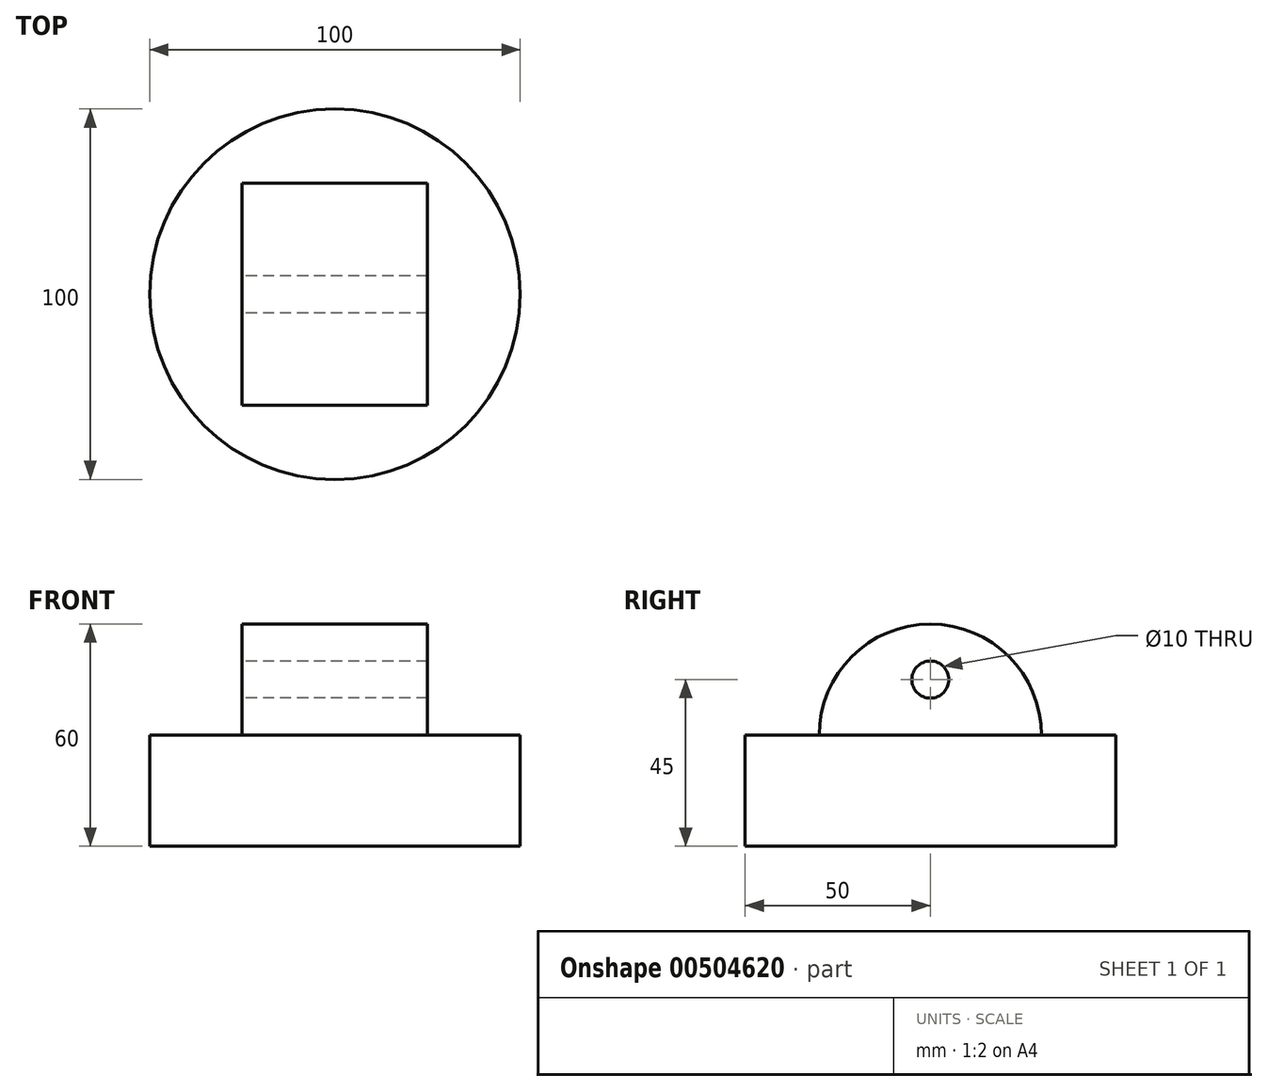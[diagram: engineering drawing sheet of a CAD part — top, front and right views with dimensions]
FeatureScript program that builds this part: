
annotation { "Feature Type Name" : "Feature", "Feature Type Description" : "" }
export const myFeature = defineFeature(function(context is Context, id is Id, definition is map)
    precondition{}
    {
        {
            var Q0;
            Q0=qCreatedBy(makeId("Top.planeOp"),FACE);
            var sketch = newSketch(context, id + "F0", { "sketchPlane" : qUnion([Q0])});
            skCircle(sketch, "E0", {"center": v(0, 0) * mm, "radius": 50 * mm});
            skLineSegment(sketch, "E1", {"start": v(0, 0) * mm, "end": v(0, 50) * mm});
            skSolve(sketch);
        }
        {
            var Q0;
            Q0=qSketchRegion(id+"F0",true);
            extrude(context, id + "F1", {"entities" : qUnion([Q0]), "depth" : 30 * mm});
        }
        {
            var Q0;
            Q0=qCreatedBy(makeId("Right.planeOp"),FACE);
            var sketch = newSketch(context, id + "F2", { "sketchPlane" : qUnion([Q0])});
            skCircle(sketch, "E2", {"center": v(0, 30) * mm, "radius": 30 * mm});
            skLineSegment(sketch, "E3", {"start": v(0, 30) * mm, "end": v(-30, 30) * mm});
            skLineSegment(sketch, "E4", {"start": v(0, 30) * mm, "end": v(0, 45) * mm});
            skCircle(sketch, "E5", {"center": v(0, 45) * mm, "radius": 5 * mm});
            skLineSegment(sketch, "E6", {"start": v(0, 45) * mm, "end": v(5, 45) * mm});
            skSolve(sketch);
        }
        {
            var Q0;
            Q0=qSketchRegion(id+"F2",true);
            extrude(context, id + "F3", {"entities" : qUnion([Q0]), "operationType" : NewBodyOperationType.ADD, "depth" : 25 * mm, "hasSecondDirection" : true, "secondDirectionOppositeDirection" : true, "secondDirectionDepth" : 25 * mm, "offsetDistance" : 25 * mm});
        }
    });
